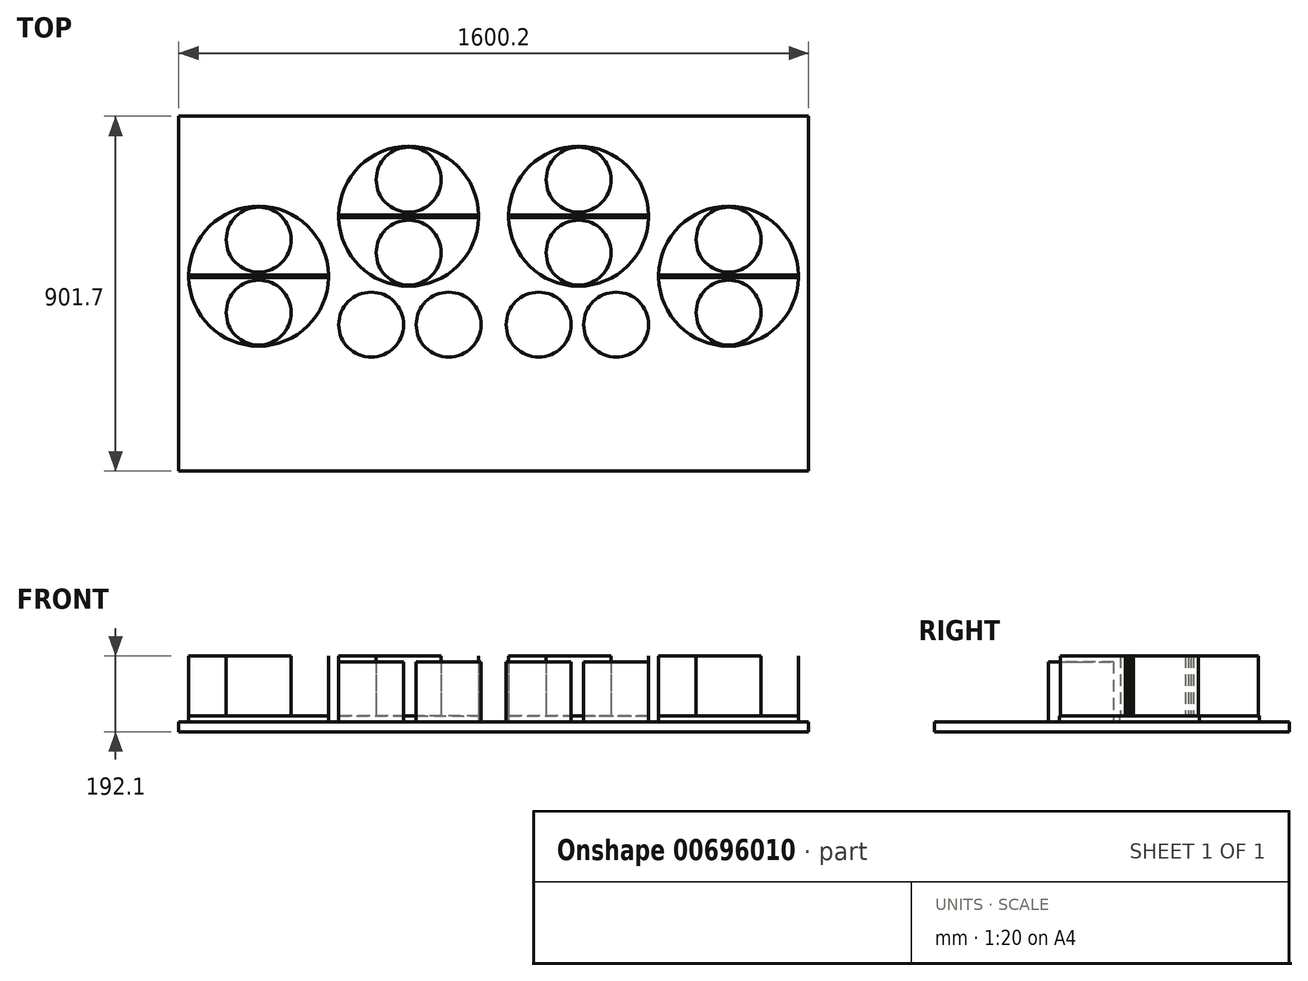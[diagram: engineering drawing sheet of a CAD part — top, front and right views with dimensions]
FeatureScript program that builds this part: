
annotation { "Feature Type Name" : "Feature", "Feature Type Description" : "" }
export const myFeature = defineFeature(function(context is Context, id is Id, definition is map)
    precondition{}
    {
        {
            var Q0;
            Q0=qCreatedBy(makeId("Top.planeOp"),FACE);
            var sketch = newSketch(context, id + "F0", { "sketchPlane" : qUnion([Q0])});
            skLineSegment(sketch, "E0.bottom", {"start": v(-800.1, 0) * mm, "end": v(800.1, 0) * mm});
            skLineSegment(sketch, "E0.top", {"start": v(-800.1, -901.7) * mm, "end": v(800.1, -901.7) * mm});
            skLineSegment(sketch, "E0.left", {"start": v(-800.1, 0) * mm, "end": v(-800.1, -901.7) * mm});
            skLineSegment(sketch, "E0.right", {"start": v(800.1, 0) * mm, "end": v(800.1, -901.7) * mm});
            skSolve(sketch);
        }
        {
            var Q0;
            Q0 = qSketchRegion(id + "F0", true);
            extrude(context, id + "F1", {"entities" : qUnion([Q0]), "oppositeDirection" : true, "depth" : 25.4 * mm, "offsetDistance" : 25.4 * mm});
        }
        {
            var Q0;
            Q0=makeQuery(id+"F1.opExtrude","CAP_FACE",FACE,{"disambiguationData":[OSD([sQuery(id+"F0.wireOp",EDGE,"E0.bottom"),sQuery(id+"F0.wireOp",EDGE,"E0.top"),sQuery(id+"F0.wireOp",EDGE,"E0.left"),sQuery(id+"F0.wireOp",EDGE,"E0.right")])],"isStart":true});
            var sketch = newSketch(context, id + "F2", { "sketchPlane" : qUnion([Q0])});
            skCircle(sketch, "E1", {"center": v(-596.9, -406.4) * mm, "radius": 177.8 * mm});
            skCircle(sketch, "E2", {"center": v(-215.9, -254) * mm, "radius": 177.8 * mm});
            skLineSegment(sketch, "E3", {"start": v(0, -18.56) * mm, "end": v(0, -901.7) * mm, "construction": true});
            skLineSegment(sketch, "E4", {"start": v(0, -673.1) * mm, "end": v(-1016, -673.1) * mm, "construction": true});
            skCircle(sketch, "E5.MirrorC", {"center": v(215.9, -254) * mm, "radius": 177.8 * mm});
            skCircle(sketch, "E6.MirrorC", {"center": v(596.9, -406.4) * mm, "radius": 177.8 * mm});
            skSolve(sketch);
        }
        {
            var Q0;
            Q0 = qSketchRegion(id + "F2", true);
            extrude(context, id + "F3", {"entities" : qUnion([Q0]), "operationType" : NewBodyOperationType.ADD, "depth" : 14.3 * mm, "offsetDistance" : 25.4 * mm});
        }
        {
            var Q0;
            Q0=makeQuery(id+"F3.opExtrude","CAP_FACE",FACE,{"disambiguationData":[OSD([sQuery(id+"F2.wireOp",EDGE,"E2")])],"isStart":false});
            var sketch = newSketch(context, id + "F4", { "sketchPlane" : qUnion([Q0])});
            skLineSegment(sketch, "E7", {"start": v(0, 0) * mm, "end": v(0, -974.91) * mm, "construction": true});
            skLineSegment(sketch, "E8.bottom", {"start": v(-419.13, -403.22) * mm, "end": v(-774.67, -403.22) * mm});
            skLineSegment(sketch, "E8.top", {"start": v(-419.13, -409.57) * mm, "end": v(-774.67, -409.57) * mm});
            skLineSegment(sketch, "E8.left", {"start": v(-419.13, -403.22) * mm, "end": v(-419.13, -409.57) * mm});
            skLineSegment(sketch, "E8.right", {"start": v(-774.67, -403.22) * mm, "end": v(-774.67, -409.57) * mm});
            skPoint(sketch, "E8.middle", {"position": v(-596.9, -406.4) * mm});
            skLineSegment(sketch, "E9.bottom", {"start": v(-38.13, -250.83) * mm, "end": v(-393.67, -250.83) * mm});
            skLineSegment(sketch, "E9.top", {"start": v(-38.13, -257.18) * mm, "end": v(-393.67, -257.18) * mm});
            skLineSegment(sketch, "E9.left", {"start": v(-38.13, -250.83) * mm, "end": v(-38.13, -257.18) * mm});
            skLineSegment(sketch, "E9.right", {"start": v(-393.67, -250.83) * mm, "end": v(-393.67, -257.18) * mm});
            skPoint(sketch, "E9.middle", {"position": v(-215.9, -254) * mm});
            skLineSegment(sketch, "E10.MirrorCS", {"start": v(38.13, -250.83) * mm, "end": v(393.67, -250.83) * mm});
            skLineSegment(sketch, "E11.MirrorCS", {"start": v(38.13, -257.18) * mm, "end": v(393.67, -257.18) * mm});
            skLineSegment(sketch, "E12.MirrorCS", {"start": v(393.67, -250.83) * mm, "end": v(393.67, -257.18) * mm});
            skLineSegment(sketch, "E13.MirrorCS", {"start": v(38.13, -250.83) * mm, "end": v(38.13, -257.18) * mm});
            skLineSegment(sketch, "E14.MirrorCS", {"start": v(419.13, -409.57) * mm, "end": v(774.67, -409.57) * mm});
            skLineSegment(sketch, "E15.MirrorCS", {"start": v(419.13, -403.22) * mm, "end": v(774.67, -403.22) * mm});
            skLineSegment(sketch, "E16.MirrorCS", {"start": v(419.13, -403.22) * mm, "end": v(419.13, -409.57) * mm});
            skLineSegment(sketch, "E17.MirrorCS", {"start": v(774.67, -403.22) * mm, "end": v(774.67, -409.57) * mm});
            skCircle(sketch, "E18", {"center": v(-596.9, -499.11) * mm, "radius": 82.55 * mm});
            skCircle(sketch, "E19", {"center": v(-596.9, -313.7) * mm, "radius": 82.55 * mm});
            skCircle(sketch, "E20", {"center": v(-215.9, -161.29) * mm, "radius": 82.55 * mm});
            skCircle(sketch, "E21", {"center": v(-215.9, -346.71) * mm, "radius": 82.55 * mm});
            skCircle(sketch, "E22.MirrorC", {"center": v(215.9, -346.71) * mm, "radius": 82.55 * mm});
            skCircle(sketch, "E23.MirrorC", {"center": v(215.9, -161.29) * mm, "radius": 82.55 * mm});
            skCircle(sketch, "E24.MirrorC", {"center": v(596.9, -313.7) * mm, "radius": 82.55 * mm});
            skCircle(sketch, "E25.MirrorC", {"center": v(596.9, -499.11) * mm, "radius": 82.55 * mm});
            skSolve(sketch);
        }
        {
            var Q0;
            Q0 = qSketchRegion(id + "F4", true);
            extrude(context, id + "F5", {"entities" : qUnion([Q0]), "operationType" : NewBodyOperationType.ADD, "depth" : 152.4 * mm, "offsetDistance" : 25.4 * mm});
        }
        {
            var Q0;
            Q0=makeQuery(id+"F1.opExtrude","CAP_FACE",FACE,{"disambiguationData":[OSD([sQuery(id+"F0.wireOp",EDGE,"E0.bottom"),sQuery(id+"F0.wireOp",EDGE,"E0.top"),sQuery(id+"F0.wireOp",EDGE,"E0.left"),sQuery(id+"F0.wireOp",EDGE,"E0.right")])],"isStart":true});
            var sketch = newSketch(context, id + "F6", { "sketchPlane" : qUnion([Q0])});
            skLineSegment(sketch, "E26", {"start": v(0, 0) * mm, "end": v(0, -1016) * mm, "construction": true});
            skLineSegment(sketch, "E27", {"start": v(0, -647.7) * mm, "end": v(-762, -647.7) * mm, "construction": true});
            skCircle(sketch, "E28", {"center": v(-311.15, -529.6) * mm, "radius": 82.55 * mm});
            skCircle(sketch, "E29", {"center": v(-114.3, -529.6) * mm, "radius": 82.55 * mm});
            skCircle(sketch, "E30.MirrorC", {"center": v(114.3, -529.6) * mm, "radius": 82.55 * mm});
            skCircle(sketch, "E31.MirrorC", {"center": v(311.15, -529.6) * mm, "radius": 82.55 * mm});
            skSolve(sketch);
        }
        {
            var Q0;
            Q0 = qSketchRegion(id + "F6", true);
            extrude(context, id + "F7", {"entities" : qUnion([Q0]), "operationType" : NewBodyOperationType.ADD, "depth" : 152.4 * mm, "offsetDistance" : 25.4 * mm});
        }
    });
